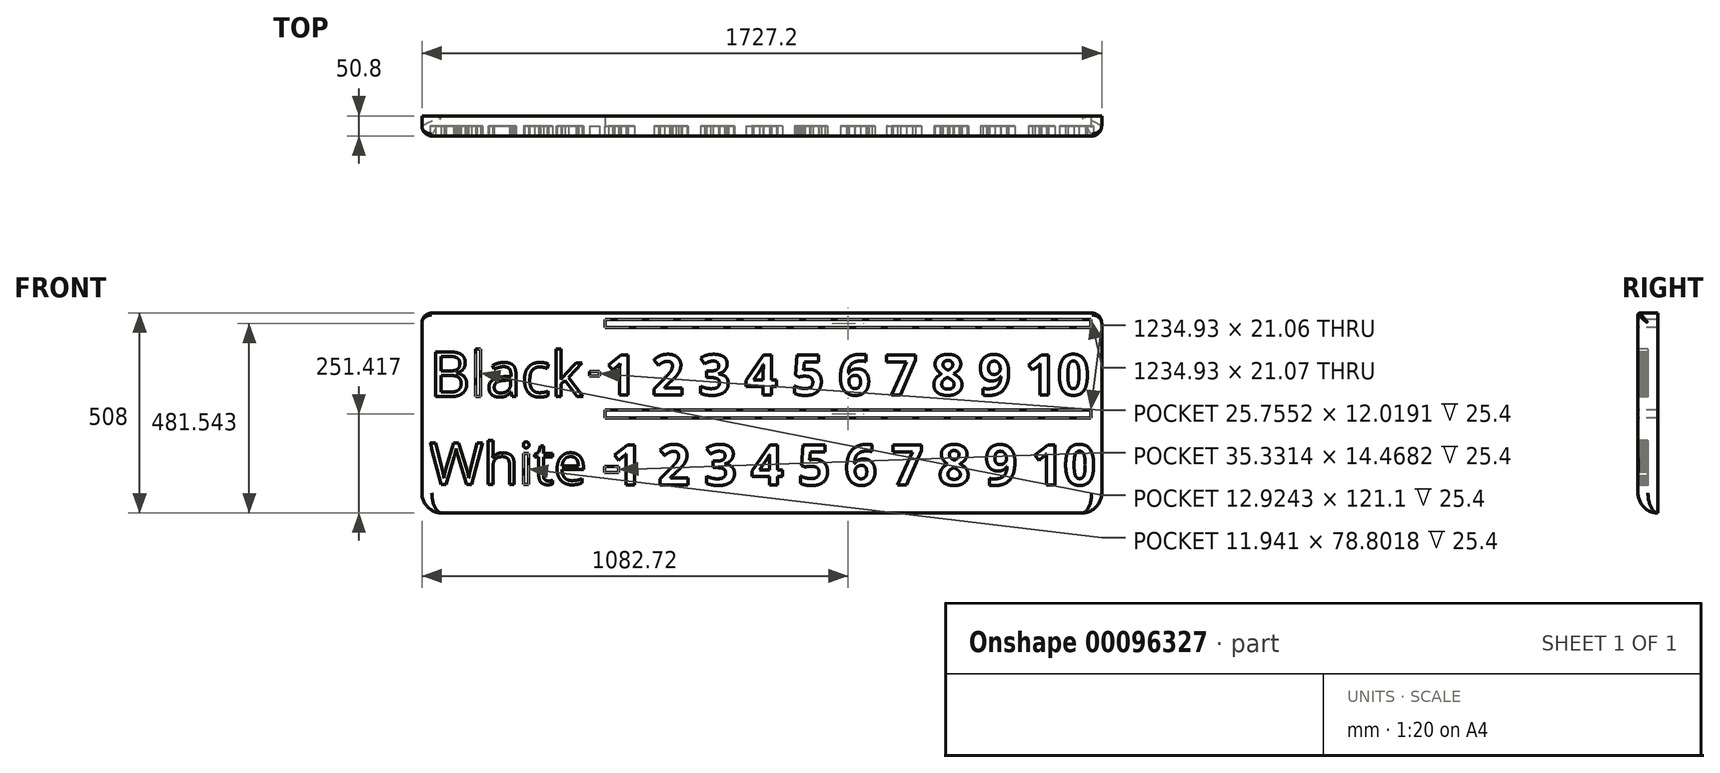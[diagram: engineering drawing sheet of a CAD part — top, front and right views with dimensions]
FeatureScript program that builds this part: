
annotation { "Feature Type Name" : "Feature", "Feature Type Description" : "" }
export const myFeature = defineFeature(function(context is Context, id is Id, definition is map)
    precondition{}
    {
        {
            var Q0;
            Q0=qCreatedBy(makeId("Front.planeOp"),FACE);
            var sketch = newSketch(context, id + "F0", { "sketchPlane" : qUnion([Q0])});
            skLineSegment(sketch, "E0", {"start": v(-967.63, 135.4) * mm, "end": v(759.57, 135.4) * mm});
            skLineSegment(sketch, "E1", {"start": v(-967.63, 135.4) * mm, "end": v(-967.63, -372.6) * mm});
            skLineSegment(sketch, "E2", {"start": v(-967.63, -372.6) * mm, "end": v(759.57, -372.6) * mm});
            skLineSegment(sketch, "E3", {"start": v(759.57, -372.6) * mm, "end": v(759.57, 135.4) * mm});
            skSolve(sketch);
        }
        {
            var Q0;
            Q0 = qSketchRegion(id + "F0", true);
            extrude(context, id + "F1", {"entities" : qUnion([Q0]), "depth" : 50.8 * mm});
        }
        {
            var Q0;
            {var subQ0=sQuery(id+"F0.wireOp",EDGE,"E0");var subQ1=sQuery(id+"F0.wireOp",EDGE,"E2");var subQ2=sQuery(id+"F0.wireOp",EDGE,"E1");var subQ3=sQuery(id+"F0.wireOp",EDGE,"E3");Q0=makeQuery(id+"F1U2y3EFPMNAUuD_1.boolean.opBoolean","SPLIT",FACE,{"disambiguationData":[TD([makeQuery(id+"F1.opExtrude","SWEPT_FACE",FACE,{"disambiguationData":[OSD([subQ0])]})])],"derivedFrom":makeQuery(id+"F1.opExtrude","CAP_FACE",FACE,{"disambiguationData":[OSD([subQ0,subQ2,subQ1,subQ3])],"isStart":false})});}
            var sketch = newSketch(context, id + "F2", { "sketchPlane" : qUnion([Q0])});
            skLineSegment(sketch, "E4", {"start": v(-502.38, 119.47) * mm, "end": v(732.55, 119.47) * mm});
            skLineSegment(sketch, "E5", {"start": v(732.55, 119.47) * mm, "end": v(732.55, 98.4) * mm});
            skLineSegment(sketch, "E6", {"start": v(732.55, 98.4) * mm, "end": v(-502.38, 98.4) * mm});
            skLineSegment(sketch, "E7", {"start": v(-502.38, 98.4) * mm, "end": v(-502.38, 119.47) * mm});
            skSolve(sketch);
        }
        {
            var Q0;
            Q0 = qSketchRegion(id + "F2", true);
            extrude(context, id + "F3", {"entities" : qUnion([Q0]), "operationType" : NewBodyOperationType.REMOVE, "endBound" : BoundingType.THROUGH_ALL, "oppositeDirection" : true, "depth" : 25.4 * mm});
        }
        {
            var Q0;
            {var subQ0=sQuery(id+"F0.wireOp",EDGE,"E0");var subQ1=sQuery(id+"F0.wireOp",EDGE,"E2");var subQ2=sQuery(id+"F0.wireOp",EDGE,"E1");var subQ3=sQuery(id+"F0.wireOp",EDGE,"E3");Q0=makeQuery(id+"F1U2y3EFPMNAUuD_1.boolean.opBoolean","SPLIT",FACE,{"disambiguationData":[TD([makeQuery(id+"F1.opExtrude","SWEPT_FACE",FACE,{"disambiguationData":[OSD([subQ0])]})])],"derivedFrom":makeQuery(id+"F1.opExtrude","CAP_FACE",FACE,{"disambiguationData":[OSD([subQ0,subQ2,subQ1,subQ3])],"isStart":false})});}
            var sketch = newSketch(context, id + "F4", { "sketchPlane" : qUnion([Q0])});
            skLineSegment(sketch, "E8", {"start": v(-502.38, -110.66) * mm, "end": v(732.55, -110.66) * mm});
            skLineSegment(sketch, "E9", {"start": v(732.55, -110.66) * mm, "end": v(732.55, -131.72) * mm});
            skLineSegment(sketch, "E10", {"start": v(732.55, -131.72) * mm, "end": v(-502.38, -131.72) * mm});
            skLineSegment(sketch, "E11", {"start": v(-502.38, -131.72) * mm, "end": v(-502.38, -110.66) * mm});
            skSolve(sketch);
        }
        {
            var Q0;
            Q0 = qSketchRegion(id + "F4", true);
            extrude(context, id + "F5", {"entities" : qUnion([Q0]), "operationType" : NewBodyOperationType.REMOVE, "endBound" : BoundingType.THROUGH_ALL, "oppositeDirection" : true, "depth" : 25.4 * mm});
        }
        {
            var Q0;
            {var subQ0=sQuery(id+"F0.wireOp",EDGE,"E0");var subQ1=sQuery(id+"F0.wireOp",EDGE,"E2");var subQ2=sQuery(id+"F0.wireOp",EDGE,"E1");var subQ3=sQuery(id+"F0.wireOp",EDGE,"E3");Q0=makeQuery(id+"F1U2y3EFPMNAUuD_1.boolean.opBoolean","SPLIT",FACE,{"disambiguationData":[TD([makeQuery(id+"F1.opExtrude","SWEPT_FACE",FACE,{"disambiguationData":[OSD([subQ0])]})])],"derivedFrom":makeQuery(id+"F1.opExtrude","CAP_FACE",FACE,{"disambiguationData":[OSD([subQ0,subQ2,subQ1,subQ3])],"isStart":false})});}
            var sketch = newSketch(context, id + "F6", { "sketchPlane" : qUnion([Q0])});
            skText(sketch, "E12", { "text": "1 2 3 4 5 6 7 8 9 10", "fontName": "OpenSans-Bold.ttf"});
            const initialGuessF6  = {"E12": [-0.50238, -0.0726, 1, 0, 0.10283]};
            skSetInitialGuess(sketch, initialGuessF6);
            skSolve(sketch);
        }
        {
            var Q0;
            Q0 = qSketchRegion(id + "F6", true);
            extrude(context, id + "F7", {"entities" : qUnion([Q0]), "operationType" : NewBodyOperationType.REMOVE, "oppositeDirection" : true, "depth" : 25.4 * mm});
        }
        {
            var Q0;
            {var subQ4=sQuery(id+"F0.wireOp",EDGE,"E2");var subQ7=sQuery(id+"F0.wireOp",EDGE,"E1");var subQ9=sQuery(id+"F0.wireOp",EDGE,"E3");var subQ12=sQuery(id+"F0.wireOp",EDGE,"E0");var subQ13=makeQuery(id+"F1.opExtrude","SWEPT_FACE",FACE,{"disambiguationData":[OSD([subQ12])]});Q0=makeQuery(id+"F7.boolean.opBoolean","SPLIT",FACE,{"disambiguationData":[TD([subQ13])],"derivedFrom":makeQuery(id+"F1U2y3EFPMNAUuD_1.boolean.opBoolean","SPLIT",FACE,{"disambiguationData":[TD([subQ13])],"derivedFrom":makeQuery(id+"F1.opExtrude","CAP_FACE",FACE,{"disambiguationData":[OSD([subQ12,subQ7,subQ4,subQ9])],"isStart":false})})});}
            var sketch = newSketch(context, id + "F8", { "sketchPlane" : qUnion([Q0])});
            skText(sketch, "E13", { "text": "1 2 3 4 5 6 7 8 9 10", "fontName": "OpenSans-Bold.ttf"});
            const initialGuessF8  = {"E13": [-0.48671, -0.3015, 1, 0, 0.10285]};
            skSetInitialGuess(sketch, initialGuessF8);
            skSolve(sketch);
        }
        {
            var Q0;
            Q0 = qSketchRegion(id + "F8", true);
            extrude(context, id + "F9", {"entities" : qUnion([Q0]), "operationType" : NewBodyOperationType.REMOVE, "oppositeDirection" : true, "depth" : 25.4 * mm});
        }
        {
            var Q0;
            {var subQ100=sQuery(id+"F0.wireOp",EDGE,"E3");var subQ109=sQuery(id+"F0.wireOp",EDGE,"E2");var subQ124=sQuery(id+"F0.wireOp",EDGE,"E0");var subQ125=makeQuery(id+"F1.opExtrude","SWEPT_FACE",FACE,{"disambiguationData":[OSD([subQ124])]});var subQ138=sQuery(id+"F0.wireOp",EDGE,"E1");Q0=makeQuery(id+"F9.boolean.opBoolean","SPLIT",FACE,{"disambiguationData":[TD([subQ125])],"derivedFrom":makeQuery(id+"F7.boolean.opBoolean","SPLIT",FACE,{"disambiguationData":[TD([subQ125])],"derivedFrom":makeQuery(id+"F1U2y3EFPMNAUuD_1.boolean.opBoolean","SPLIT",FACE,{"disambiguationData":[TD([subQ125])],"derivedFrom":makeQuery(id+"F1.opExtrude","CAP_FACE",FACE,{"disambiguationData":[OSD([subQ124,subQ138,subQ109,subQ100])],"isStart":false})})})});}
            var sketch = newSketch(context, id + "F10", { "sketchPlane" : qUnion([Q0])});
            skLineSegment(sketch, "E14.bottom", {"start": v(-541.57, -24.56) * mm, "end": v(-515.8, -24.56) * mm});
            skLineSegment(sketch, "E14.top", {"start": v(-541.57, -12.54) * mm, "end": v(-515.8, -12.54) * mm});
            skLineSegment(sketch, "E14.left", {"start": v(-541.57, -24.56) * mm, "end": v(-541.57, -12.54) * mm});
            skLineSegment(sketch, "E14.right", {"start": v(-515.8, -24.56) * mm, "end": v(-515.8, -12.54) * mm});
            skSolve(sketch);
        }
        {
            var Q0;
            Q0 = qSketchRegion(id + "F10", true);
            extrude(context, id + "F11", {"entities" : qUnion([Q0]), "operationType" : NewBodyOperationType.REMOVE, "oppositeDirection" : true, "depth" : 25.4 * mm});
        }
        {
            var Q0;
            {var subQ100=sQuery(id+"F0.wireOp",EDGE,"E3");var subQ109=sQuery(id+"F0.wireOp",EDGE,"E2");var subQ124=sQuery(id+"F0.wireOp",EDGE,"E0");var subQ125=makeQuery(id+"F1.opExtrude","SWEPT_FACE",FACE,{"disambiguationData":[OSD([subQ124])]});var subQ138=sQuery(id+"F0.wireOp",EDGE,"E1");Q0=makeQuery(id+"F9.boolean.opBoolean","SPLIT",FACE,{"disambiguationData":[TD([subQ125])],"derivedFrom":makeQuery(id+"F7.boolean.opBoolean","SPLIT",FACE,{"disambiguationData":[TD([subQ125])],"derivedFrom":makeQuery(id+"F1U2y3EFPMNAUuD_1.boolean.opBoolean","SPLIT",FACE,{"disambiguationData":[TD([subQ125])],"derivedFrom":makeQuery(id+"F1.opExtrude","CAP_FACE",FACE,{"disambiguationData":[OSD([subQ124,subQ138,subQ109,subQ100])],"isStart":false})})})});}
            var sketch = newSketch(context, id + "F12", { "sketchPlane" : qUnion([Q0])});
            skLineSegment(sketch, "E15.bottom", {"start": v(-503.2, -269.48) * mm, "end": v(-467.87, -269.48) * mm});
            skLineSegment(sketch, "E15.top", {"start": v(-503.2, -255.01) * mm, "end": v(-467.87, -255.01) * mm});
            skLineSegment(sketch, "E15.left", {"start": v(-503.2, -255.01) * mm, "end": v(-503.2, -269.48) * mm});
            skLineSegment(sketch, "E15.right", {"start": v(-467.87, -255.01) * mm, "end": v(-467.87, -269.48) * mm});
            skSolve(sketch);
        }
        {
            var Q0;
            Q0 = qSketchRegion(id + "F12", true);
            extrude(context, id + "F13", {"entities" : qUnion([Q0]), "operationType" : NewBodyOperationType.REMOVE, "oppositeDirection" : true, "depth" : 25.4 * mm});
        }
        {
            var Q0;
            {var subQ118=sQuery(id+"F0.wireOp",EDGE,"E0");var subQ119=makeQuery(id+"F1.opExtrude","SWEPT_FACE",FACE,{"disambiguationData":[OSD([subQ118])]});var subQ135=sQuery(id+"F0.wireOp",EDGE,"E1");var subQ146=sQuery(id+"F0.wireOp",EDGE,"E2");var subQ154=sQuery(id+"F0.wireOp",EDGE,"E3");Q0=makeQuery(id+"FRZpzfPGdSZMUAi_1.boolean.opBoolean","MERGE",FACE,{"derivedFrom":[makeQuery(id+"F9.boolean.opBoolean","SPLIT",FACE,{"disambiguationData":[TD([subQ119])],"derivedFrom":makeQuery(id+"F7.boolean.opBoolean","SPLIT",FACE,{"disambiguationData":[TD([subQ119])],"derivedFrom":makeQuery(id+"F1.opExtrude","CAP_FACE",FACE,{"disambiguationData":[OSD([subQ118,subQ135,subQ146,subQ154])],"isStart":false})})}),makeQuery(id+"FRZpzfPGdSZMUAi_1.opExtrude","CAP_FACE",FACE,{"disambiguationData":[OSD([sQuery(id+"Fo0TTmm3As3Cg3R_1.wireOp",EDGE,"yO0obYRg-k93A-RoeO-azBA-Dn1ouCjgvAPI"),sQuery(id+"Fo0TTmm3As3Cg3R_1.wireOp",EDGE,"szN1noRC-FSMT-I5YT-YCNM-NcqK6YIxlKz0"),sQuery(id+"Fo0TTmm3As3Cg3R_1.wireOp",EDGE,"CsIcFXdl-mCst-QybS-htSQ-EBUZP0JRVDkf"),sQuery(id+"Fo0TTmm3As3Cg3R_1.wireOp",EDGE,"BCU2wRvl-glJ8-5PUv-0VL3-gR4ALEGQXY9s"),sQuery(id+"Fo0TTmm3As3Cg3R_1.wireOp",EDGE,"ruR0pWgU-GCiY-Jnsu-FT2O-yPlVVPXKl60I"),sQuery(id+"Fo0TTmm3As3Cg3R_1.wireOp",EDGE,"Lb523tHs-o3CZ-aZN1-8cki-G17cuXQTESo9"),sQuery(id+"Fo0TTmm3As3Cg3R_1.wireOp",EDGE,"1sEJMOGa-ObH7-p6qa-uiwy-ISjAk2YeN7ub"),sQuery(id+"Fo0TTmm3As3Cg3R_1.wireOp",EDGE,"MmtIBD8y-ovlG-HkYy-Ziye-pE9ZkjFIHIp4"),sQuery(id+"Fo0TTmm3As3Cg3R_1.wireOp",EDGE,"zwYWQc0C-vynI-XIlI-H5nH-nnZE0v61jBnb"),sQuery(id+"Fo0TTmm3As3Cg3R_1.wireOp",EDGE,"iZd5akgK-0x2v-s4M5-7uBV-3RRXDkd9gayQ")])],"isStart":true})]});}
            var sketch = newSketch(context, id + "F14", { "sketchPlane" : qUnion([Q0])});
            skSolve(sketch);
        }
        {
            var Q0;
            Q0=makeQuery(id+"F14.imprint","IMPRINT",FACE,{"disambiguationData":[TD([[makeQuery(id+"F14.imprint","IMPRINT",EDGE,{"derivedFrom":makeQuery(id+"F1.opExtrude","CAP_EDGE",EDGE,{"disambiguationData":[OSD([sQuery(id+"F0.wireOp",EDGE,"E0")])],"isStart":false})}),-1.0]])]});
            var sketch = newSketch(context, id + "F15", { "sketchPlane" : qUnion([Q0])});
            skText(sketch, "E16", { "text": "Black", "fontName": "OpenSans-Regular.ttf"});
            skText(sketch, "E17", { "text": "White", "fontName": "OpenSans-Regular.ttf"});
            const initialGuessF15  = {"E16": [-0.94812, -0.07683, 1, 0, 0.11475], "E17": [-0.94812, -0.29961, 1, 0, 0.10602]};
            skSetInitialGuess(sketch, initialGuessF15);
            skSolve(sketch);
        }
        {
            var Q0;
            Q0 = qSketchRegion(id + "F15", true);
            extrude(context, id + "F16", {"entities" : qUnion([Q0]), "operationType" : NewBodyOperationType.REMOVE, "oppositeDirection" : true, "depth" : 25.4 * mm});
        }
        {
            var Q0;
            Q0=makeQuery(id+"F1.opExtrude","CAP_EDGE",EDGE,{"disambiguationData":[OSD([sQuery(id+"F0.wireOp",EDGE,"E0")])],"isStart":false});
            fillet(context, id + "F17", {"entities" : qUnion([Q0]), "radius" : 5.08 * mm, "tangentPropagation" : true, "allowEdgeOverflow" : false});
        }
        {
            var Q0;
            Q0=makeQuery(id+"F1.opExtrude","CAP_EDGE",EDGE,{"disambiguationData":[OSD([sQuery(id+"F0.wireOp",EDGE,"E1")])],"isStart":false});
            fillet(context, id + "F18", {"entities" : qUnion([Q0]), "radius" : 25.4 * mm, "tangentPropagation" : true, "allowEdgeOverflow" : false});
        }
        {
            var Q0;
            Q0=makeQuery(id+"F1.opExtrude","CAP_EDGE",EDGE,{"disambiguationData":[OSD([sQuery(id+"F0.wireOp",EDGE,"E3")])],"isStart":false});
            fillet(context, id + "F19", {"entities" : qUnion([Q0]), "radius" : 25.4 * mm, "tangentPropagation" : true, "allowEdgeOverflow" : false});
        }
        {
            var Q0;
            Q0=makeQuery(id+"F1.opExtrude","CAP_EDGE",EDGE,{"disambiguationData":[OSD([sQuery(id+"F0.wireOp",EDGE,"E2")])],"isStart":false});
            fillet(context, id + "F20", {"entities" : qUnion([Q0]), "radius" : 50.8 * mm, "tangentPropagation" : true, "allowEdgeOverflow" : false});
        }
    });
